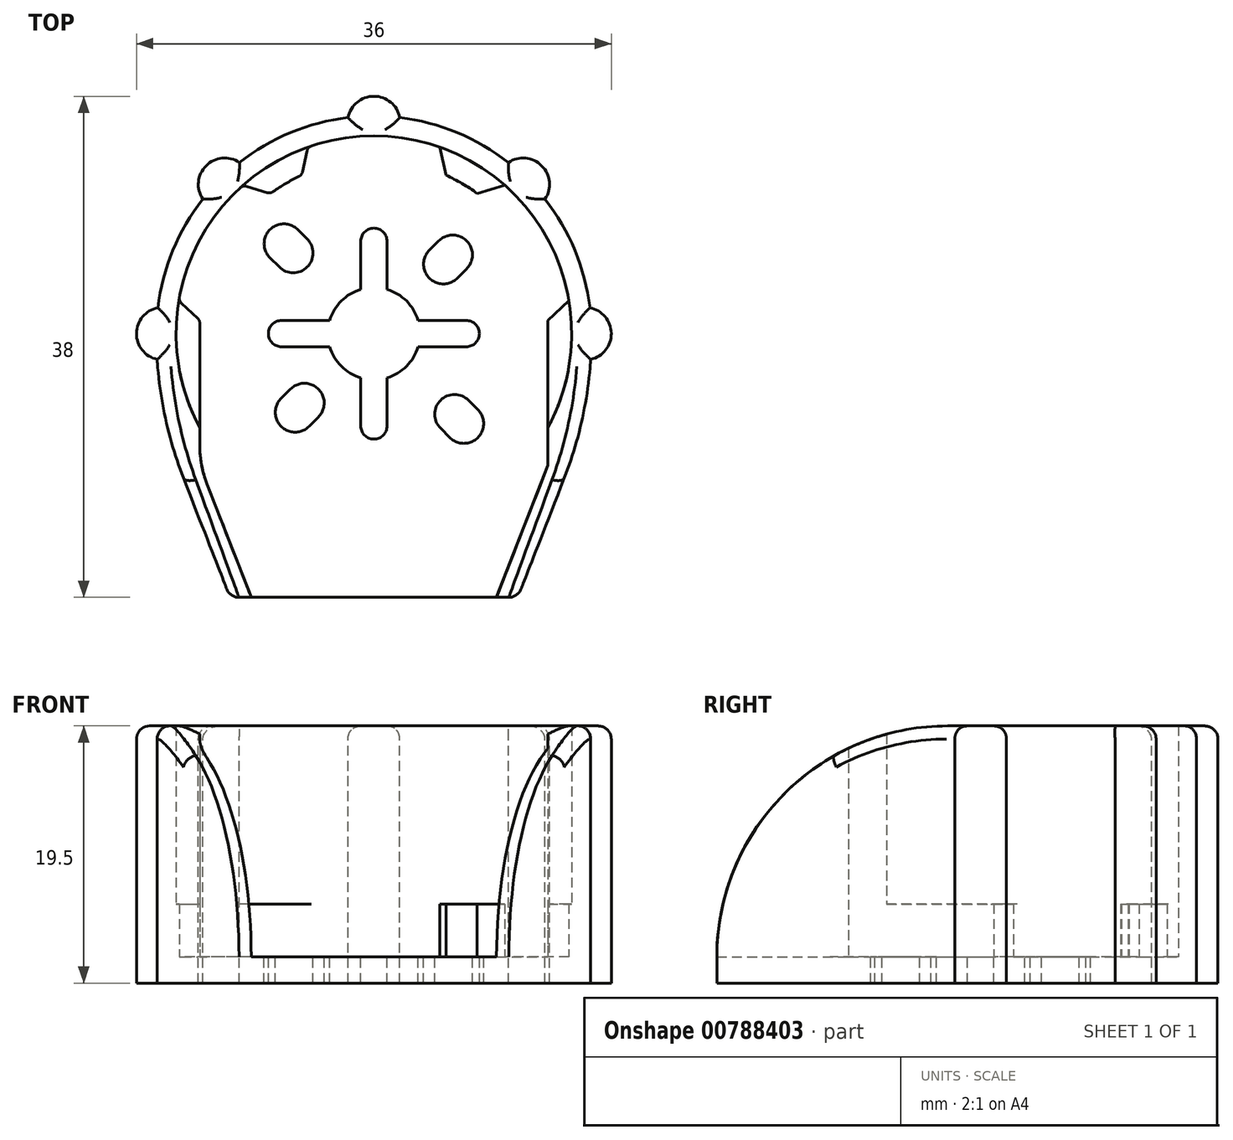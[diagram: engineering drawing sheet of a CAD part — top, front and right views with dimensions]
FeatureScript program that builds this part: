
annotation { "Feature Type Name" : "Feature", "Feature Type Description" : "" }
export const myFeature = defineFeature(function(context is Context, id is Id, definition is map)
    precondition{}
    {
        {
            var Q0;
            Q0=qCreatedBy(makeId("Top.planeOp"),FACE);
            var sketch = newSketch(context, id + "F0", { "sketchPlane" : qUnion([Q0])});
            skLineSegment(sketch, "E0", {"start": v(-9.3, -20) * mm, "end": v(-13.2, -10) * mm});
            skLineSegment(sketch, "E1", {"start": v(-13.2, -10) * mm, "end": v(-13.2, 1) * mm});
            skArc(sketch, "E2", {"start": v(0, 15) * mm, "mid": v(-2.54, 14.78) * mm, "end": v(-5, 14.14) * mm});
            skLineSegment(sketch, "E3", {"start": v(0, 0) * mm, "end": v(0, 15) * mm, "construction": true});
            skLineSegment(sketch, "E4", {"start": v(0, 0) * mm, "end": v(-5, 14.14) * mm, "construction": true});
            skArc(sketch, "E5", {"start": v(-9.92, 11.25) * mm, "mid": v(-13.1, 7.3) * mm, "end": v(-14.8, 2.5) * mm});
            skLineSegment(sketch, "E6", {"start": v(0, 0) * mm, "end": v(-9.92, 11.25) * mm, "construction": true});
            skLineSegment(sketch, "E7", {"start": v(0, 0) * mm, "end": v(-14.8, 2.5) * mm, "construction": true});
            skArc(sketch, "E8", {"start": v(-5.47, 12.01) * mm, "mid": v(-6.7, 11.38) * mm, "end": v(-7.83, 10.62) * mm});
            skLineSegment(sketch, "E9", {"start": v(-5.47, 12.01) * mm, "end": v(0, 0) * mm, "construction": true});
            skLineSegment(sketch, "E10", {"start": v(-7.83, 10.62) * mm, "end": v(0, 0) * mm, "construction": true});
            skLineSegment(sketch, "E11", {"start": v(-5.47, 12.01) * mm, "end": v(-5, 14.14) * mm});
            skLineSegment(sketch, "E12", {"start": v(-7.83, 10.62) * mm, "end": v(-9.92, 11.25) * mm});
            skLineSegment(sketch, "E13", {"start": v(-14.8, 2.5) * mm, "end": v(-13.2, 1) * mm});
            skArc(sketch, "E14", {"start": v(0, 3.5) * mm, "mid": v(-0.5, 3.46) * mm, "end": v(-1, 3.35) * mm, "construction": true});
            skLineSegment(sketch, "E15", {"start": v(-3.35, 1) * mm, "end": v(-7, 1) * mm});
            skLineSegment(sketch, "E16", {"start": v(-7, 1) * mm, "end": v(-7, -1) * mm, "construction": true});
            skLineSegment(sketch, "E17", {"start": v(-7, -1) * mm, "end": v(-3.35, -1) * mm});
            skLineSegment(sketch, "E18", {"start": v(0, 0) * mm, "end": v(-34.13, 0) * mm, "construction": true});
            skArc(sketch, "E19", {"start": v(-7, 1) * mm, "mid": v(-8, 0) * mm, "end": v(-7, -1) * mm});
            skArc(sketch, "E20", {"start": v(-3.35, 1) * mm, "mid": v(-3.5, 0) * mm, "end": v(-3.35, -1) * mm, "construction": true});
            skArc(sketch, "E21", {"start": v(-3.35, -1) * mm, "mid": v(-2.47, -2.47) * mm, "end": v(-1, -3.35) * mm});
            skLineSegment(sketch, "E22", {"start": v(-1, 3.35) * mm, "end": v(-1, 7) * mm});
            skArc(sketch, "E23", {"start": v(0, 8) * mm, "mid": v(-0.7, 7.7) * mm, "end": v(-1, 7) * mm});
            skArc(sketch, "E24", {"start": v(-1, 3.35) * mm, "mid": v(-2.47, 2.47) * mm, "end": v(-3.35, 1) * mm});
            skLineSegment(sketch, "E25.MirrorCS", {"start": v(-1, -3.35) * mm, "end": v(-1, -7) * mm});
            skArc(sketch, "E26.MirrorCS", {"start": v(0, -8) * mm, "mid": v(-0.7, -7.7) * mm, "end": v(-1, -7) * mm});
            skArc(sketch, "E27", {"start": v(-1, -3.35) * mm, "mid": v(-0.5, -3.46) * mm, "end": v(0, -3.5) * mm, "construction": true});
            skLineSegment(sketch, "E28", {"start": v(0, 0) * mm, "end": v(-30.92, 30.92) * mm, "construction": true});
            skLineSegment(sketch, "E29", {"start": v(0, 0) * mm, "end": v(-31.07, -31.07) * mm, "construction": true});
            skLineSegment(sketch, "E30.bottom", {"start": v(-5.76, 7.88) * mm, "end": v(-5.76, 7.88) * mm});
            skLineSegment(sketch, "E30.top", {"start": v(-7.88, 5.76) * mm, "end": v(-7.18, 5.06) * mm});
            skLineSegment(sketch, "E30.left", {"start": v(-5.76, 7.88) * mm, "end": v(-7.88, 5.76) * mm, "construction": true});
            skLineSegment(sketch, "E30.right", {"start": v(-5.06, 7.18) * mm, "end": v(-7.18, 5.06) * mm, "construction": true});
            skLineSegment(sketch, "E31", {"start": v(-5.76, 7.88) * mm, "end": v(-5.06, 7.18) * mm});
            skArc(sketch, "E32", {"start": v(-5.76, 7.88) * mm, "mid": v(-7.88, 7.88) * mm, "end": v(-7.88, 5.76) * mm});
            skArc(sketch, "E33", {"start": v(-7.18, 5.06) * mm, "mid": v(-5.06, 5.06) * mm, "end": v(-5.06, 7.18) * mm});
            skLineSegment(sketch, "E34.bottom", {"start": v(-7.04, -4.91) * mm, "end": v(-6.33, -4.2) * mm});
            skLineSegment(sketch, "E34.top", {"start": v(-4.91, -7.04) * mm, "end": v(-4.2, -6.33) * mm});
            skLineSegment(sketch, "E34.left", {"start": v(-7.04, -4.91) * mm, "end": v(-4.91, -7.04) * mm, "construction": true});
            skLineSegment(sketch, "E34.right", {"start": v(-6.33, -4.2) * mm, "end": v(-4.2, -6.33) * mm, "construction": true});
            skArc(sketch, "E35", {"start": v(-4.2, -6.33) * mm, "mid": v(-4.2, -4.2) * mm, "end": v(-6.33, -4.2) * mm});
            skArc(sketch, "E36", {"start": v(-7.04, -4.91) * mm, "mid": v(-7.04, -7.04) * mm, "end": v(-4.91, -7.04) * mm});
            skLineSegment(sketch, "E37", {"start": v(-9.3, -20) * mm, "end": v(0, -20) * mm});
            skArc(sketch, "E38", {"start": v(0, 16.5) * mm, "mid": v(-0.98, 16.47) * mm, "end": v(-1.96, 16.38) * mm, "construction": true});
            skLineSegment(sketch, "E39", {"start": v(-10.91, -20) * mm, "end": v(-9.3, -20) * mm});
            skArc(sketch, "E40", {"start": v(-10.2, 12.97) * mm, "mid": v(-12.73, 12.73) * mm, "end": v(-12.97, 10.2) * mm});
            skArc(sketch, "E41", {"start": v(-10.2, 12.97) * mm, "mid": v(-11.67, 11.67) * mm, "end": v(-12.97, 10.2) * mm, "construction": true});
            skArc(sketch, "E42", {"start": v(-12.97, 10.2) * mm, "mid": v(-15.24, 6.31) * mm, "end": v(-16.38, 1.96) * mm});
            skArc(sketch, "E43", {"start": v(-16.5, 0) * mm, "mid": v(-16.48, -0.98) * mm, "end": v(-16.44, -1.95) * mm, "construction": true});
            skLineSegment(sketch, "E44", {"start": v(-10.91, -20) * mm, "end": v(-14.44, -10.95) * mm});
            skArc(sketch, "E45", {"start": v(-16.38, 1.96) * mm, "mid": v(-18, 0.03) * mm, "end": v(-16.44, -1.95) * mm});
            skArc(sketch, "E46", {"start": v(-16.38, 1.96) * mm, "mid": v(-16.47, 0.98) * mm, "end": v(-16.5, 0) * mm, "construction": true});
            skArc(sketch, "E47", {"start": v(-16.44, -1.95) * mm, "mid": v(-15.78, -6.53) * mm, "end": v(-14.44, -10.95) * mm});
            skArc(sketch, "E48", {"start": v(0, 18) * mm, "mid": v(-1.27, 17.54) * mm, "end": v(-1.96, 16.38) * mm});
            skArc(sketch, "E49", {"start": v(-1.96, 16.38) * mm, "mid": v(-6.31, 15.24) * mm, "end": v(-10.2, 12.97) * mm});
            skArc(sketch, "E50.MirrorCS", {"start": v(3.35, 1) * mm, "mid": v(3.5, 0) * mm, "end": v(3.35, -1) * mm, "construction": true});
            skArc(sketch, "E51.MirrorCS", {"start": v(5.47, 12.01) * mm, "mid": v(6.7, 11.38) * mm, "end": v(7.83, 10.62) * mm});
            skLineSegment(sketch, "E52.MirrorCS", {"start": v(7.83, 10.62) * mm, "end": v(9.92, 11.25) * mm});
            skLineSegment(sketch, "E53.MirrorCS", {"start": v(7, 1) * mm, "end": v(7, -1) * mm, "construction": true});
            skArc(sketch, "E54.MirrorCS", {"start": v(16.5, 0) * mm, "mid": v(16.48, -0.98) * mm, "end": v(16.44, -1.95) * mm, "construction": true});
            skArc(sketch, "E55.MirrorCS", {"start": v(0, 3.5) * mm, "mid": v(0.5, 3.46) * mm, "end": v(1, 3.35) * mm, "construction": true});
            skLineSegment(sketch, "E56.MirrorCS", {"start": v(5.47, 12.01) * mm, "end": v(5, 14.14) * mm});
            skArc(sketch, "E57.MirrorCS", {"start": v(1, -3.35) * mm, "mid": v(0.5, -3.46) * mm, "end": v(0, -3.5) * mm, "construction": true});
            skArc(sketch, "E58.MirrorCS", {"start": v(16.38, 1.96) * mm, "mid": v(16.47, 0.98) * mm, "end": v(16.5, 0) * mm, "construction": true});
            skArc(sketch, "E59.MirrorCS", {"start": v(10.2, 12.97) * mm, "mid": v(11.67, 11.67) * mm, "end": v(12.97, 10.2) * mm, "construction": true});
            skArc(sketch, "E60.MirrorCS", {"start": v(0, 16.5) * mm, "mid": v(0.98, 16.47) * mm, "end": v(1.96, 16.38) * mm, "construction": true});
            skArc(sketch, "E61.MirrorCS", {"start": v(0, 8) * mm, "mid": v(0.7, 7.7) * mm, "end": v(1, 7) * mm});
            skLineSegment(sketch, "E62.MirrorCS", {"start": v(10.91, -20) * mm, "end": v(9.3, -20) * mm});
            skLineSegment(sketch, "E63.MirrorCS", {"start": v(14.8, 2.5) * mm, "end": v(13.2, 1) * mm});
            skArc(sketch, "E64.MirrorCS", {"start": v(0, -8) * mm, "mid": v(0.7, -7.7) * mm, "end": v(1, -7) * mm});
            skArc(sketch, "E65.MirrorCS", {"start": v(0, 18) * mm, "mid": v(1.27, 17.54) * mm, "end": v(1.96, 16.38) * mm});
            skArc(sketch, "E66.MirrorCS", {"start": v(7, 1) * mm, "mid": v(8, 0) * mm, "end": v(7, -1) * mm});
            skLineSegment(sketch, "E67.MirrorCS", {"start": v(7, -1) * mm, "end": v(3.35, -1) * mm});
            skLineSegment(sketch, "E68.MirrorCS", {"start": v(1, 3.35) * mm, "end": v(1, 7) * mm});
            skArc(sketch, "E69.MirrorCS", {"start": v(3.35, -1) * mm, "mid": v(2.47, -2.47) * mm, "end": v(1, -3.35) * mm});
            skLineSegment(sketch, "E70.MirrorCS", {"start": v(3.35, 1) * mm, "end": v(7, 1) * mm});
            skArc(sketch, "E71.MirrorCS", {"start": v(10.2, 12.97) * mm, "mid": v(12.73, 12.73) * mm, "end": v(12.97, 10.2) * mm});
            skLineSegment(sketch, "E72.MirrorCS", {"start": v(13.2, -10) * mm, "end": v(13.2, 1) * mm});
            skLineSegment(sketch, "E73.MirrorCS", {"start": v(0, 0) * mm, "end": v(31.07, -31.07) * mm, "construction": true});
            skArc(sketch, "E74.MirrorCS", {"start": v(16.44, -1.95) * mm, "mid": v(15.78, -6.53) * mm, "end": v(14.44, -10.95) * mm});
            skLineSegment(sketch, "E75.MirrorCS", {"start": v(0, 0) * mm, "end": v(30.92, 30.92) * mm, "construction": true});
            skLineSegment(sketch, "E76.MirrorCS", {"start": v(0, 0) * mm, "end": v(9.92, 11.25) * mm, "construction": true});
            skLineSegment(sketch, "E77.MirrorCS", {"start": v(0, 0) * mm, "end": v(14.8, 2.5) * mm, "construction": true});
            skArc(sketch, "E78.MirrorCS", {"start": v(12.97, 10.2) * mm, "mid": v(15.24, 6.31) * mm, "end": v(16.38, 1.96) * mm});
            skArc(sketch, "E79.MirrorCS", {"start": v(1.96, 16.38) * mm, "mid": v(6.31, 15.24) * mm, "end": v(10.2, 12.97) * mm});
            skLineSegment(sketch, "E80.MirrorCS", {"start": v(7.83, 10.62) * mm, "end": v(0, 0) * mm, "construction": true});
            skLineSegment(sketch, "E81.MirrorCS", {"start": v(9.3, -20) * mm, "end": v(0, -20) * mm});
            skArc(sketch, "E82.MirrorCS", {"start": v(0, 15) * mm, "mid": v(2.54, 14.78) * mm, "end": v(5, 14.14) * mm});
            skArc(sketch, "E83.MirrorCS", {"start": v(1, 3.35) * mm, "mid": v(2.47, 2.47) * mm, "end": v(3.35, 1) * mm});
            skArc(sketch, "E84.MirrorCS", {"start": v(16.38, 1.96) * mm, "mid": v(18, 0.03) * mm, "end": v(16.44, -1.95) * mm});
            skLineSegment(sketch, "E85.MirrorCS", {"start": v(10.91, -20) * mm, "end": v(14.44, -10.95) * mm});
            skLineSegment(sketch, "E86.MirrorCS", {"start": v(1, -3.35) * mm, "end": v(1, -7) * mm});
            skLineSegment(sketch, "E87.MirrorCS", {"start": v(0, 0) * mm, "end": v(34.13, 0) * mm, "construction": true});
            skLineSegment(sketch, "E88.MirrorCS", {"start": v(0, 0) * mm, "end": v(5, 14.14) * mm, "construction": true});
            skArc(sketch, "E89.MirrorCS", {"start": v(9.92, 11.25) * mm, "mid": v(13.1, 7.3) * mm, "end": v(14.8, 2.5) * mm});
            skLineSegment(sketch, "E90.MirrorCS", {"start": v(5.47, 12.01) * mm, "end": v(0, 0) * mm, "construction": true});
            skLineSegment(sketch, "E91.MirrorCS", {"start": v(9.3, -20) * mm, "end": v(13.2, -10) * mm});
            skArc(sketch, "E92.MirrorCS", {"start": v(4.91, 7.04) * mm, "mid": v(7.04, 7.04) * mm, "end": v(7.04, 4.91) * mm});
            skLineSegment(sketch, "E93.MirrorCS", {"start": v(4.91, 7.04) * mm, "end": v(4.2, 6.33) * mm});
            skArc(sketch, "E94.MirrorCS", {"start": v(6.33, 4.2) * mm, "mid": v(4.2, 4.2) * mm, "end": v(4.2, 6.33) * mm});
            skLineSegment(sketch, "E95.MirrorCS", {"start": v(7.04, 4.91) * mm, "end": v(6.33, 4.2) * mm});
            skArc(sketch, "E96.MirrorCS", {"start": v(7.88, -5.76) * mm, "mid": v(7.88, -7.88) * mm, "end": v(5.76, -7.88) * mm});
            skLineSegment(sketch, "E97.MirrorCS", {"start": v(5.76, -7.88) * mm, "end": v(5.06, -7.18) * mm});
            skArc(sketch, "E98.MirrorCS", {"start": v(5.06, -7.18) * mm, "mid": v(5.06, -5.06) * mm, "end": v(7.18, -5.06) * mm});
            skLineSegment(sketch, "E99.MirrorCS", {"start": v(7.88, -5.76) * mm, "end": v(7.18, -5.06) * mm});
            skSolve(sketch);
        }
        {
            var Q0;
            Q0=makeQuery(id+"F0.imprint","IMPRINT",FACE,{"disambiguationData":[TD([[makeQuery(id+"F0.imprint","IMPRINT",EDGE,{"derivedFrom":sQuery(id+"F0.wireOp",EDGE,"E0")}),-1.0]])]});
            var Q1;
            Q1=makeQuery(id+"F0.imprint","IMPRINT",FACE,{"disambiguationData":[TD([[makeQuery(id+"F0.imprint","IMPRINT",EDGE,{"derivedFrom":sQuery(id+"F0.wireOp",EDGE,"E0")}),1.0]])]});
            extrude(context, id + "F1", {"entities" : qUnion([Q0, Q1]), "oppositeDirection" : true, "depth" : 2 * mm, "offsetDistance" : 25 * mm});
        }
        {
            var Q0;
            Q0=makeQuery(id+"F0.imprint","IMPRINT",FACE,{"disambiguationData":[TD([[makeQuery(id+"F0.imprint","IMPRINT",EDGE,{"derivedFrom":sQuery(id+"F0.wireOp",EDGE,"E0")}),1.0]])]});
            extrude(context, id + "F2", {"entities" : qUnion([Q0]), "operationType" : NewBodyOperationType.ADD, "depth" : 4 * mm, "offsetDistance" : 25 * mm});
        }
        {
            var Q0;
            Q0=makeQuery(id+"F2.opExtrude","CAP_FACE",FACE,{"disambiguationData":[OSD([sQuery(id+"F0.wireOp",EDGE,"E0"),sQuery(id+"F0.wireOp",EDGE,"E1"),sQuery(id+"F0.wireOp",EDGE,"E2"),sQuery(id+"F0.wireOp",EDGE,"E5"),sQuery(id+"F0.wireOp",EDGE,"E8"),sQuery(id+"F0.wireOp",EDGE,"E11"),sQuery(id+"F0.wireOp",EDGE,"E12"),sQuery(id+"F0.wireOp",EDGE,"E13"),sQuery(id+"F0.wireOp",EDGE,"E38"),sQuery(id+"F0.wireOp",EDGE,"E39"),sQuery(id+"F0.wireOp",EDGE,"E40"),sQuery(id+"F0.wireOp",EDGE,"E42"),sQuery(id+"F0.wireOp",EDGE,"E43"),sQuery(id+"F0.wireOp",EDGE,"E44"),sQuery(id+"F0.wireOp",EDGE,"c7bc9f34-3f87-4cef-8f49-272cc0f19f1f1.MirrorCS"),sQuery(id+"F0.wireOp",EDGE,"c7bc9f34-3f87-4cef-8f49-272cc0f19f1f10.MirrorCS"),sQuery(id+"F0.wireOp",EDGE,"c7bc9f34-3f87-4cef-8f49-272cc0f19f1f11.MirrorCS"),sQuery(id+"F0.wireOp",EDGE,"c7bc9f34-3f87-4cef-8f49-272cc0f19f1f14.MirrorCS"),sQuery(id+"F0.wireOp",EDGE,"c7bc9f34-3f87-4cef-8f49-272cc0f19f1f15.MirrorCS"),sQuery(id+"F0.wireOp",EDGE,"c7bc9f34-3f87-4cef-8f49-272cc0f19f1f29.MirrorCS"),sQuery(id+"F0.wireOp",EDGE,"c7bc9f34-3f87-4cef-8f49-272cc0f19f1f32.MirrorCS"),sQuery(id+"F0.wireOp",EDGE,"c7bc9f34-3f87-4cef-8f49-272cc0f19f1f35.MirrorCS"),sQuery(id+"F0.wireOp",EDGE,"c7bc9f34-3f87-4cef-8f49-272cc0f19f1f36.MirrorCS"),sQuery(id+"F0.wireOp",EDGE,"c7bc9f34-3f87-4cef-8f49-272cc0f19f1f39.MirrorCS"),sQuery(id+"F0.wireOp",EDGE,"c7bc9f34-3f87-4cef-8f49-272cc0f19f1f40.MirrorCS"),sQuery(id+"F0.wireOp",EDGE,"c7bc9f34-3f87-4cef-8f49-272cc0f19f1f45.MirrorCS"),sQuery(id+"F0.wireOp",EDGE,"c7bc9f34-3f87-4cef-8f49-272cc0f19f1f47.MirrorCS"),sQuery(id+"F0.wireOp",EDGE,"c7bc9f34-3f87-4cef-8f49-272cc0f19f1f49.MirrorCS")])],"isStart":false});
            var sketch = newSketch(context, id + "F3", { "sketchPlane" : qUnion([Q0])});
            skCircle(sketch, "E100", {"center": v(0, 0) * mm, "radius": 15 * mm});
            skSolve(sketch);
        }
        {
            var Q0;
            {var subQ0=makeQuery(id+"F2.opExtrude","CAP_EDGE",EDGE,{"disambiguationData":[OSD([sQuery(id+"F0.wireOp",EDGE,"E0")])],"isStart":false});Q0=makeQuery(id+"F3.imprint","IMPRINT",FACE,{"disambiguationData":[TD([[makeQuery(id+"F3.imprint","IMPRINT",EDGE,{"derivedFrom":subQ0}),1.0]])]});}
            extrude(context, id + "F4", {"entities" : qUnion([Q0]), "operationType" : NewBodyOperationType.ADD, "depth" : 13.5 * mm, "offsetDistance" : 25 * mm});
        }
        {
            var Q0;
            Q0=qCreatedBy(makeId("Right.planeOp"),FACE);
            var sketch = newSketch(context, id + "F5", { "sketchPlane" : qUnion([Q0])});
            skPoint(sketch, "E101.0", {"position": v(-20, 17.5) * mm});
            skPoint(sketch, "E102.0", {"position": v(-20, 0) * mm});
            skLineSegment(sketch, "E103", {"start": v(-20, 17.5) * mm, "end": v(-4.21, 17.5) * mm, "construction": true});
            skLineSegment(sketch, "E104", {"start": v(-20, 0) * mm, "end": v(-20, -4.35) * mm, "construction": true});
            skArc(sketch, "E105", {"start": v(-2.5, 17.5) * mm, "mid": v(-14.87, 12.37) * mm, "end": v(-20, 0) * mm});
            skLineSegment(sketch, "E106", {"start": v(-2.5, 17.5) * mm, "end": v(-2.5, 20.87) * mm});
            skLineSegment(sketch, "E107", {"start": v(-2.5, 20.87) * mm, "end": v(-23.91, 20.87) * mm});
            skLineSegment(sketch, "E108", {"start": v(-23.91, 20.87) * mm, "end": v(-23.91, 0) * mm});
            skLineSegment(sketch, "E109", {"start": v(-23.91, 0) * mm, "end": v(-20, 0) * mm});
            skSolve(sketch);
        }
        {
            var Q0;
            Q0=makeQuery(id+"F5.imprint","IMPRINT",FACE,{"disambiguationData":[TD([[makeQuery(id+"F5.imprint","IMPRINT",EDGE,{"derivedFrom":sQuery(id+"F5.wireOp",EDGE,"E105")}),-1.0]])]});
            extrude(context, id + "F6", {"entities" : qUnion([Q0]), "operationType" : NewBodyOperationType.REMOVE, "depth" : 50 * mm, "offsetDistance" : 25 * mm, "symmetric" : true});
        }
        {
            var Q0;
            {var subQ0=sQuery(id+"F0.wireOp",EDGE,"E1");var subQ1=sQuery(id+"F0.wireOp",EDGE,"E0");Q0=makeQuery(id+"F4.boolean.opBoolean","MERGE",EDGE,{"derivedFrom":[makeQuery(id+"F2.opExtrude","SWEPT_EDGE",EDGE,{"disambiguationData":[OSD([subQ1,subQ0])]}),makeQuery(id+"F4.opExtrude","SWEPT_EDGE",EDGE,{"disambiguationData":[OSD([subQ1,subQ0])]})]});}
            var Q1;
            {var subQ0=sQuery(id+"F0.wireOp",EDGE,"c7bc9f34-3f87-4cef-8f49-272cc0f19f1f39.MirrorCS");var subQ1=sQuery(id+"F0.wireOp",EDGE,"c7bc9f34-3f87-4cef-8f49-272cc0f19f1f36.MirrorCS");Q1=makeQuery(id+"F4.boolean.opBoolean","MERGE",EDGE,{"derivedFrom":[makeQuery(id+"F2.opExtrude","SWEPT_EDGE",EDGE,{"disambiguationData":[OSD([subQ1,subQ0])]}),makeQuery(id+"F4.opExtrude","SWEPT_EDGE",EDGE,{"disambiguationData":[OSD([subQ1,subQ0])]})]});}
            fillet(context, id + "F7", {"entities" : qUnion([Q0, Q1]), "radius" : 8 * mm, "tangentPropagation" : true, "allowEdgeOverflow" : false});
        }
        {
            var Q0;
            Q0=makeQuery(id+"F2.opExtrude","SWEPT_EDGE",EDGE,{"disambiguationData":[OSD([sQuery(id+"F0.wireOp",EDGE,"E1"),sQuery(id+"F0.wireOp",EDGE,"E13")])]});
            var Q1;
            Q1=makeQuery(id+"F2.opExtrude","SWEPT_EDGE",EDGE,{"disambiguationData":[OSD([sQuery(id+"F0.wireOp",EDGE,"E5"),sQuery(id+"F0.wireOp",EDGE,"E13")])]});
            var Q2;
            Q2=makeQuery(id+"F2.opExtrude","SWEPT_EDGE",EDGE,{"disambiguationData":[OSD([sQuery(id+"F0.wireOp",EDGE,"E5"),sQuery(id+"F0.wireOp",EDGE,"E12")])]});
            var Q3;
            Q3=makeQuery(id+"F2.opExtrude","SWEPT_EDGE",EDGE,{"disambiguationData":[OSD([sQuery(id+"F0.wireOp",EDGE,"E8"),sQuery(id+"F0.wireOp",EDGE,"E12")])]});
            var Q4;
            Q4=makeQuery(id+"F2.opExtrude","SWEPT_EDGE",EDGE,{"disambiguationData":[OSD([sQuery(id+"F0.wireOp",EDGE,"E8"),sQuery(id+"F0.wireOp",EDGE,"E11")])]});
            var Q5;
            Q5=makeQuery(id+"F2.opExtrude","SWEPT_EDGE",EDGE,{"disambiguationData":[OSD([sQuery(id+"F0.wireOp",EDGE,"E2"),sQuery(id+"F0.wireOp",EDGE,"E11")])]});
            var Q6;
            Q6=makeQuery(id+"F2.opExtrude","SWEPT_EDGE",EDGE,{"disambiguationData":[OSD([sQuery(id+"F0.wireOp",EDGE,"c7bc9f34-3f87-4cef-8f49-272cc0f19f1f11.MirrorCS"),sQuery(id+"F0.wireOp",EDGE,"c7bc9f34-3f87-4cef-8f49-272cc0f19f1f35.MirrorCS")])]});
            var Q7;
            Q7=makeQuery(id+"F2.opExtrude","SWEPT_EDGE",EDGE,{"disambiguationData":[OSD([sQuery(id+"F0.wireOp",EDGE,"c7bc9f34-3f87-4cef-8f49-272cc0f19f1f1.MirrorCS"),sQuery(id+"F0.wireOp",EDGE,"c7bc9f34-3f87-4cef-8f49-272cc0f19f1f11.MirrorCS")])]});
            var Q8;
            Q8=makeQuery(id+"F2.opExtrude","SWEPT_EDGE",EDGE,{"disambiguationData":[OSD([sQuery(id+"F0.wireOp",EDGE,"c7bc9f34-3f87-4cef-8f49-272cc0f19f1f1.MirrorCS"),sQuery(id+"F0.wireOp",EDGE,"c7bc9f34-3f87-4cef-8f49-272cc0f19f1f10.MirrorCS")])]});
            var Q9;
            Q9=makeQuery(id+"F2.opExtrude","SWEPT_EDGE",EDGE,{"disambiguationData":[OSD([sQuery(id+"F0.wireOp",EDGE,"c7bc9f34-3f87-4cef-8f49-272cc0f19f1f10.MirrorCS"),sQuery(id+"F0.wireOp",EDGE,"c7bc9f34-3f87-4cef-8f49-272cc0f19f1f40.MirrorCS")])]});
            var Q10;
            Q10=makeQuery(id+"F2.opExtrude","SWEPT_EDGE",EDGE,{"disambiguationData":[OSD([sQuery(id+"F0.wireOp",EDGE,"c7bc9f34-3f87-4cef-8f49-272cc0f19f1f14.MirrorCS"),sQuery(id+"F0.wireOp",EDGE,"c7bc9f34-3f87-4cef-8f49-272cc0f19f1f36.MirrorCS")])]});
            var Q11;
            Q11=makeQuery(id+"F2.opExtrude","SWEPT_EDGE",EDGE,{"disambiguationData":[OSD([sQuery(id+"F0.wireOp",EDGE,"c7bc9f34-3f87-4cef-8f49-272cc0f19f1f14.MirrorCS"),sQuery(id+"F0.wireOp",EDGE,"c7bc9f34-3f87-4cef-8f49-272cc0f19f1f40.MirrorCS")])]});
            fillet(context, id + "F8", {"entities" : qUnion([Q0, Q1, Q2, Q3, Q4, Q5, Q6, Q7, Q8, Q9, Q10, Q11]), "radius" : 0.5 * mm, "tangentPropagation" : true, "allowEdgeOverflow" : false});
        }
        {
            var Q0;
            {var subQ0=sQuery(id+"F0.wireOp",EDGE,"E85.MirrorCS");Q0=makeQuery(id+"F6.boolean.opBoolean","INTERSECT",EDGE,{"derivedFrom":[makeQuery(id+"F4.boolean.opBoolean","MERGE",FACE,{"derivedFrom":[makeQuery(id+"F2.boolean.opBoolean","MERGE",FACE,{"derivedFrom":[makeQuery(id+"F1.opExtrude","SWEPT_FACE",FACE,{"disambiguationData":[OSD([subQ0])]}),makeQuery(id+"F2.opExtrude","SWEPT_FACE",FACE,{"disambiguationData":[OSD([subQ0])]})]}),makeQuery(id+"F4.opExtrude","SWEPT_FACE",FACE,{"disambiguationData":[OSD([subQ0])]})]}),makeQuery(id+"F6.opExtrude","SWEPT_FACE",FACE,{"disambiguationData":[OSD([sQuery(id+"F5.wireOp",EDGE,"E105")])]})]});}
            var Q1;
            {var subQ0=sQuery(id+"F0.wireOp",EDGE,"E74.MirrorCS");Q1=makeQuery(id+"F6.boolean.opBoolean","INTERSECT",EDGE,{"derivedFrom":[makeQuery(id+"F4.boolean.opBoolean","MERGE",FACE,{"derivedFrom":[makeQuery(id+"F2.boolean.opBoolean","MERGE",FACE,{"derivedFrom":[makeQuery(id+"F1.opExtrude","SWEPT_FACE",FACE,{"disambiguationData":[OSD([subQ0])]}),makeQuery(id+"F2.opExtrude","SWEPT_FACE",FACE,{"disambiguationData":[OSD([subQ0])]})]}),makeQuery(id+"F4.opExtrude","SWEPT_FACE",FACE,{"disambiguationData":[OSD([subQ0])]})]}),makeQuery(id+"F6.opExtrude","SWEPT_FACE",FACE,{"disambiguationData":[OSD([sQuery(id+"F5.wireOp",EDGE,"E105")])]})]});}
            var Q2;
            Q2=makeQuery(id+"F4.opExtrude","CAP_EDGE",EDGE,{"disambiguationData":[OSD([sQuery(id+"F0.wireOp",EDGE,"E84.MirrorCS")])],"isStart":false});
            var Q3;
            Q3=makeQuery(id+"F4.opExtrude","CAP_EDGE",EDGE,{"disambiguationData":[OSD([sQuery(id+"F0.wireOp",EDGE,"E78.MirrorCS")])],"isStart":false});
            var Q4;
            Q4=makeQuery(id+"F4.opExtrude","CAP_EDGE",EDGE,{"disambiguationData":[OSD([sQuery(id+"F0.wireOp",EDGE,"E71.MirrorCS")])],"isStart":false});
            var Q5;
            Q5=makeQuery(id+"F4.opExtrude","CAP_EDGE",EDGE,{"disambiguationData":[OSD([sQuery(id+"F0.wireOp",EDGE,"E79.MirrorCS")])],"isStart":false});
            var Q6;
            Q6=makeQuery(id+"F4.opExtrude","CAP_EDGE",EDGE,{"disambiguationData":[OSD([sQuery(id+"F0.wireOp",EDGE,"E48"),sQuery(id+"F0.wireOp",EDGE,"E65.MirrorCS")])],"isStart":false});
            var Q7;
            Q7=makeQuery(id+"F4.opExtrude","CAP_EDGE",EDGE,{"disambiguationData":[OSD([sQuery(id+"F0.wireOp",EDGE,"E49")])],"isStart":false});
            var Q8;
            Q8=makeQuery(id+"F4.opExtrude","CAP_EDGE",EDGE,{"disambiguationData":[OSD([sQuery(id+"F0.wireOp",EDGE,"E40")])],"isStart":false});
            var Q9;
            Q9=makeQuery(id+"F4.opExtrude","CAP_EDGE",EDGE,{"disambiguationData":[OSD([sQuery(id+"F0.wireOp",EDGE,"E42")])],"isStart":false});
            var Q10;
            Q10=makeQuery(id+"F4.opExtrude","CAP_EDGE",EDGE,{"disambiguationData":[OSD([sQuery(id+"F0.wireOp",EDGE,"E45")])],"isStart":false});
            var Q11;
            {var subQ0=sQuery(id+"F0.wireOp",EDGE,"E47");Q11=makeQuery(id+"F6.boolean.opBoolean","INTERSECT",EDGE,{"derivedFrom":[makeQuery(id+"F4.boolean.opBoolean","MERGE",FACE,{"derivedFrom":[makeQuery(id+"F2.boolean.opBoolean","MERGE",FACE,{"derivedFrom":[makeQuery(id+"F1.opExtrude","SWEPT_FACE",FACE,{"disambiguationData":[OSD([subQ0])]}),makeQuery(id+"F2.opExtrude","SWEPT_FACE",FACE,{"disambiguationData":[OSD([subQ0])]})]}),makeQuery(id+"F4.opExtrude","SWEPT_FACE",FACE,{"disambiguationData":[OSD([subQ0])]})]}),makeQuery(id+"F6.opExtrude","SWEPT_FACE",FACE,{"disambiguationData":[OSD([sQuery(id+"F5.wireOp",EDGE,"E105")])]})]});}
            var Q12;
            {var subQ0=sQuery(id+"F0.wireOp",EDGE,"E44");Q12=makeQuery(id+"F6.boolean.opBoolean","INTERSECT",EDGE,{"derivedFrom":[makeQuery(id+"F4.boolean.opBoolean","MERGE",FACE,{"derivedFrom":[makeQuery(id+"F2.boolean.opBoolean","MERGE",FACE,{"derivedFrom":[makeQuery(id+"F1.opExtrude","SWEPT_FACE",FACE,{"disambiguationData":[OSD([subQ0])]}),makeQuery(id+"F2.opExtrude","SWEPT_FACE",FACE,{"disambiguationData":[OSD([subQ0])]})]}),makeQuery(id+"F4.opExtrude","SWEPT_FACE",FACE,{"disambiguationData":[OSD([subQ0])]})]}),makeQuery(id+"F6.opExtrude","SWEPT_FACE",FACE,{"disambiguationData":[OSD([sQuery(id+"F5.wireOp",EDGE,"E105")])]})]});}
            fillet(context, id + "F9", {"entities" : qUnion([Q0, Q1, Q2, Q3, Q4, Q5, Q6, Q7, Q8, Q9, Q10, Q11, Q12]), "radius" : 1 * mm, "tangentPropagation" : true, "allowEdgeOverflow" : false});
        }
    });
